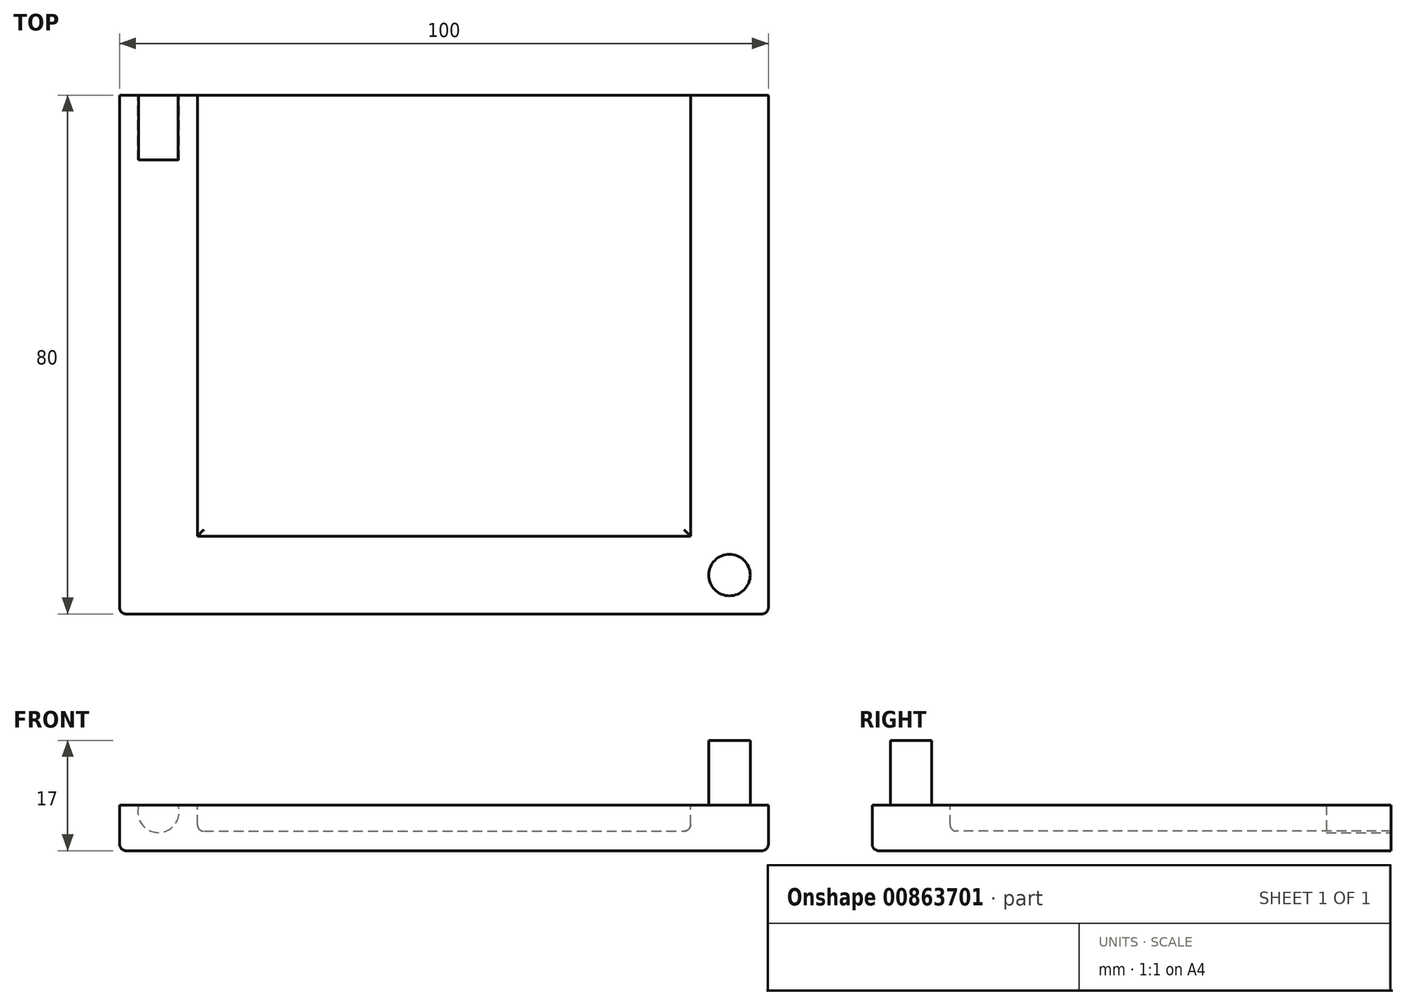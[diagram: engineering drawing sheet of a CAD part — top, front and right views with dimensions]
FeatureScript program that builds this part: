
annotation { "Feature Type Name" : "Feature", "Feature Type Description" : "" }
export const myFeature = defineFeature(function(context is Context, id is Id, definition is map)
    precondition{}
    {
        {
            var Q0;
            Q0=qCreatedBy(makeId("Top.planeOp"),FACE);
            var sketch = newSketch(context, id + "F0", { "sketchPlane" : qUnion([Q0])});
            skLineSegment(sketch, "E0.bottom", {"start": v(0, 0) * mm, "end": v(50, 0) * mm});
            skLineSegment(sketch, "E0.top", {"start": v(0, 80) * mm, "end": v(50, 80) * mm});
            skLineSegment(sketch, "E0.left", {"start": v(0, 0) * mm, "end": v(0, 80) * mm});
            skLineSegment(sketch, "E0.right", {"start": v(50, 0) * mm, "end": v(50, 80) * mm, "construction": true});
            skLineSegment(sketch, "E1.MirrorCS", {"start": v(100, 80) * mm, "end": v(50, 80) * mm});
            skLineSegment(sketch, "E2.MirrorCS", {"start": v(100, 0) * mm, "end": v(100, 80) * mm});
            skLineSegment(sketch, "E3.MirrorCS", {"start": v(100, 0) * mm, "end": v(50, 0) * mm});
            skSolve(sketch);
        }
        {
            var Q0;
            Q0=makeQuery(id+"F0.imprint","IMPRINT",FACE,{"disambiguationData":[TD([[makeQuery(id+"F0.imprint","IMPRINT",EDGE,{"derivedFrom":sQuery(id+"F0.wireOp",EDGE,"E0.bottom")}),1.0]])]});
            extrude(context, id + "F1", {"entities" : qUnion([Q0]), "depth" : 17 * mm, "offsetDistance" : 25 * mm});
        }
        {
            var Q0;
            Q0=qCreatedBy(makeId("Top.planeOp"),FACE);
            cPlane(context, id + "F2", {"entities" : qUnion([Q0]), "cplaneType" : CPlaneType.OFFSET, "offset" : 17 * mm, "width" : 150 * mm, "height" : 150 * mm});
        }
        {
            var Q0;
            Q0=qCreatedBy(id+"F2.planeOp",FACE);
            var sketch = newSketch(context, id + "F3", { "sketchPlane" : qUnion([Q0])});
            skLineSegment(sketch, "E4.bottom", {"start": v(0, 0) * mm, "end": v(50, 0) * mm});
            skLineSegment(sketch, "E4.top", {"start": v(0, 80) * mm, "end": v(50, 80) * mm});
            skLineSegment(sketch, "E4.left", {"start": v(0, 0) * mm, "end": v(0, 80) * mm});
            skLineSegment(sketch, "E4.right", {"start": v(50, 0) * mm, "end": v(50, 80) * mm, "construction": true});
            skLineSegment(sketch, "E5", {"start": v(12, 80) * mm, "end": v(12, 12) * mm});
            skLineSegment(sketch, "E6", {"start": v(12, 12) * mm, "end": v(50, 12) * mm});
            skCircle(sketch, "E7", {"center": v(6, 6) * mm, "radius": 3.2 * mm});
            skLineSegment(sketch, "E8.MirrorCS", {"start": v(88, 12) * mm, "end": v(50, 12) * mm});
            skCircle(sketch, "E9.MirrorC", {"center": v(94, 6) * mm, "radius": 3.2 * mm});
            skLineSegment(sketch, "E10.MirrorCS", {"start": v(100, 0) * mm, "end": v(100, 80) * mm});
            skLineSegment(sketch, "E11.MirrorCS", {"start": v(100, 80) * mm, "end": v(50, 80) * mm});
            skLineSegment(sketch, "E12.MirrorCS", {"start": v(100, 0) * mm, "end": v(50, 0) * mm});
            skLineSegment(sketch, "E13.MirrorCS", {"start": v(88, 80) * mm, "end": v(88, 12) * mm});
            skSolve(sketch);
        }
        {
            var Q0;
            {var subQ0=sQuery(id+"F3.wireOp",EDGE,"E5");Q0=makeQuery(id+"F3.imprint","IMPRINT",FACE,{"disambiguationData":[TD([[makeQuery(id+"F3.imprint","IMPRINT",EDGE,{"derivedFrom":subQ0}),1.0]])]});}
            extrude(context, id + "F4", {"entities" : qUnion([Q0]), "operationType" : NewBodyOperationType.REMOVE, "oppositeDirection" : true, "depth" : 14 * mm, "offsetDistance" : 25 * mm});
        }
        {
            var Q0;
            Q0=makeQuery(id+"F3.imprint","IMPRINT",FACE,{"disambiguationData":[TD([[makeQuery(id+"F3.imprint","IMPRINT",EDGE,{"derivedFrom":sQuery(id+"F3.wireOp",EDGE,"E7")}),1.0]])]});
            var Q1;
            Q1=makeQuery(id+"F3.imprint","IMPRINT",FACE,{"disambiguationData":[TD([[makeQuery(id+"F3.imprint","IMPRINT",EDGE,{"derivedFrom":sQuery(id+"F3.wireOp",EDGE,"E9.MirrorC")}),-1.0]])]});
            extrude(context, id + "F5", {"entities" : qUnion([Q0, Q1]), "operationType" : NewBodyOperationType.REMOVE, "oppositeDirection" : true, "depth" : 10 * mm, "offsetDistance" : 25 * mm});
        }
        {
            var Q0;
            Q0=qCreatedBy(makeId("Front.planeOp"),FACE);
            cPlane(context, id + "F6", {"entities" : qUnion([Q0]), "cplaneType" : CPlaneType.OFFSET, "offset" : 80 * mm, "oppositeDirection" : true, "width" : 150 * mm, "height" : 150 * mm});
        }
        {
            var Q0;
            Q0=qCreatedBy(id+"F6.planeOp",FACE);
            var sketch = newSketch(context, id + "F7", { "sketchPlane" : qUnion([Q0])});
            skCircle(sketch, "E14", {"center": v(6, 6) * mm, "radius": 3.2 * mm});
            skLineSegment(sketch, "E15", {"start": v(50, 0) * mm, "end": v(50, 32.29) * mm, "construction": true});
            skCircle(sketch, "E16.MirrorC", {"center": v(94, 6) * mm, "radius": 3.2 * mm});
            skSolve(sketch);
        }
        {
            var Q0;
            Q0=makeQuery(id+"F7.imprint","IMPRINT",FACE,{"disambiguationData":[TD([[makeQuery(id+"F7.imprint","IMPRINT",EDGE,{"derivedFrom":sQuery(id+"F7.wireOp",EDGE,"E16.MirrorC")}),-1.0]])]});
            var Q1;
            Q1=makeQuery(id+"F7.imprint","IMPRINT",FACE,{"disambiguationData":[TD([[makeQuery(id+"F7.imprint","IMPRINT",EDGE,{"derivedFrom":sQuery(id+"F7.wireOp",EDGE,"E14")}),1.0]])]});
            extrude(context, id + "F8", {"entities" : qUnion([Q0, Q1]), "operationType" : NewBodyOperationType.REMOVE, "depth" : 10 * mm, "offsetDistance" : 25 * mm});
        }
        {
            var Q0;
            Q0=makeQuery(id+"F4.boolean.opBoolean","COPY",EDGE,{"derivedFrom":makeQuery(id+"F4.opExtrude","CAP_EDGE",EDGE,{"disambiguationData":[OSD([sQuery(id+"F3.wireOp",EDGE,"E5")])],"isStart":false})});
            var Q1;
            Q1=makeQuery(id+"F4.boolean.opBoolean","COPY",EDGE,{"derivedFrom":makeQuery(id+"F4.opExtrude","CAP_EDGE",EDGE,{"disambiguationData":[OSD([sQuery(id+"F3.wireOp",EDGE,"E13.MirrorCS")])],"isStart":false})});
            var Q2;
            Q2=makeQuery(id+"F4.boolean.opBoolean","COPY",EDGE,{"derivedFrom":makeQuery(id+"F4.opExtrude","CAP_EDGE",EDGE,{"disambiguationData":[OSD([sQuery(id+"F3.wireOp",EDGE,"E6"),sQuery(id+"F3.wireOp",EDGE,"E8.MirrorCS")])],"isStart":false})});
            var Q3;
            Q3=makeQuery(id+"F5.boolean.opBoolean","COPY",EDGE,{"derivedFrom":makeQuery(id+"F5.opExtrude","CAP_EDGE",EDGE,{"disambiguationData":[OSD([sQuery(id+"F3.wireOp",EDGE,"E9.MirrorC")])],"isStart":true})});
            var Q4;
            Q4=makeQuery(id+"F5.boolean.opBoolean","COPY",EDGE,{"derivedFrom":makeQuery(id+"F5.opExtrude","CAP_EDGE",EDGE,{"disambiguationData":[OSD([sQuery(id+"F3.wireOp",EDGE,"E7")])],"isStart":true})});
            var Q5;
            Q5=makeQuery(id+"F8.boolean.opBoolean","COPY",EDGE,{"derivedFrom":makeQuery(id+"F8.opExtrude","CAP_EDGE",EDGE,{"disambiguationData":[OSD([sQuery(id+"F7.wireOp",EDGE,"E16.MirrorC")])],"isStart":true})});
            var Q6;
            Q6=makeQuery(id+"F8.boolean.opBoolean","COPY",EDGE,{"derivedFrom":makeQuery(id+"F8.opExtrude","CAP_EDGE",EDGE,{"disambiguationData":[OSD([sQuery(id+"F7.wireOp",EDGE,"E14")])],"isStart":true})});
            var Q7;
            Q7=makeQuery(id+"F1.opExtrude","CAP_EDGE",EDGE,{"disambiguationData":[OSD([sQuery(id+"F0.wireOp",EDGE,"E2.MirrorCS")])],"isStart":true});
            var Q8;
            Q8=makeQuery(id+"F1.opExtrude","CAP_EDGE",EDGE,{"disambiguationData":[OSD([sQuery(id+"F0.wireOp",EDGE,"E0.bottom"),sQuery(id+"F0.wireOp",EDGE,"E3.MirrorCS")])],"isStart":true});
            var Q9;
            Q9=makeQuery(id+"F1.opExtrude","CAP_EDGE",EDGE,{"disambiguationData":[OSD([sQuery(id+"F0.wireOp",EDGE,"E0.left")])],"isStart":true});
            var Q10;
            Q10=makeQuery(id+"F1.opExtrude","SWEPT_EDGE",EDGE,{"disambiguationData":[OSD([sQuery(id+"F0.wireOp",EDGE,"E2.MirrorCS"),sQuery(id+"F0.wireOp",EDGE,"E3.MirrorCS")])]});
            var Q11;
            Q11=makeQuery(id+"F1.opExtrude","SWEPT_EDGE",EDGE,{"disambiguationData":[OSD([sQuery(id+"F0.wireOp",EDGE,"E0.bottom"),sQuery(id+"F0.wireOp",EDGE,"E0.left")])]});
            fillet(context, id + "F9", {"entities" : qUnion([Q0, Q1, Q2, Q3, Q4, Q5, Q6, Q7, Q8, Q9, Q10, Q11]), "radius" : 1 * mm, "tangentPropagation" : true, "allowEdgeOverflow" : false});
        }
    });
